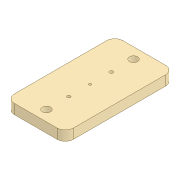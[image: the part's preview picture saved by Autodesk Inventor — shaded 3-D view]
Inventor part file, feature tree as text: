
AUTODESK INVENTOR PART (.ipt)
format: ipt  version: 2020 (Build 240168000, 168)  size: 124,416 bytes
history: native  units: mm
features: extrude x2, sketch x2, other x1, chamfer x1, fillet x1
ambient origin geometry x8: Origin, YZ Plane, XZ Plane, XY Plane, X Axis, Y Axis, Z Axis, Center Point
bodies: Body1 (feature_tree)
feature tree (7):
  other  "Sólido1"
  extrude  "Extrusão1"  Depth=12.0mm TaperAngle=0.0deg
  extrude  "Extrusão2"  Depth=10.0mm
  chamfer  "Chanfro1"  Distance=4.2mm
  fillet  "Arredondamento1"  Radius=12.0mm
  sketch  "Esboço1"  dims[d0=69.9mm d1=12.0mm d2=0.0mm]
  sketch  "Esboço2"  dims[d3=3.0mm d4=4.2mm d5=4.2mm d6=12.0mm d7=0.0mm d8=2.5mm d9=2.0mm d10=45.0deg d11=132.363mm d12=72.0mm d13=10.0mm d14=53.1mm d15=10.0mm d16=53.1mm d20=52.0mm d21=10.0mm]
